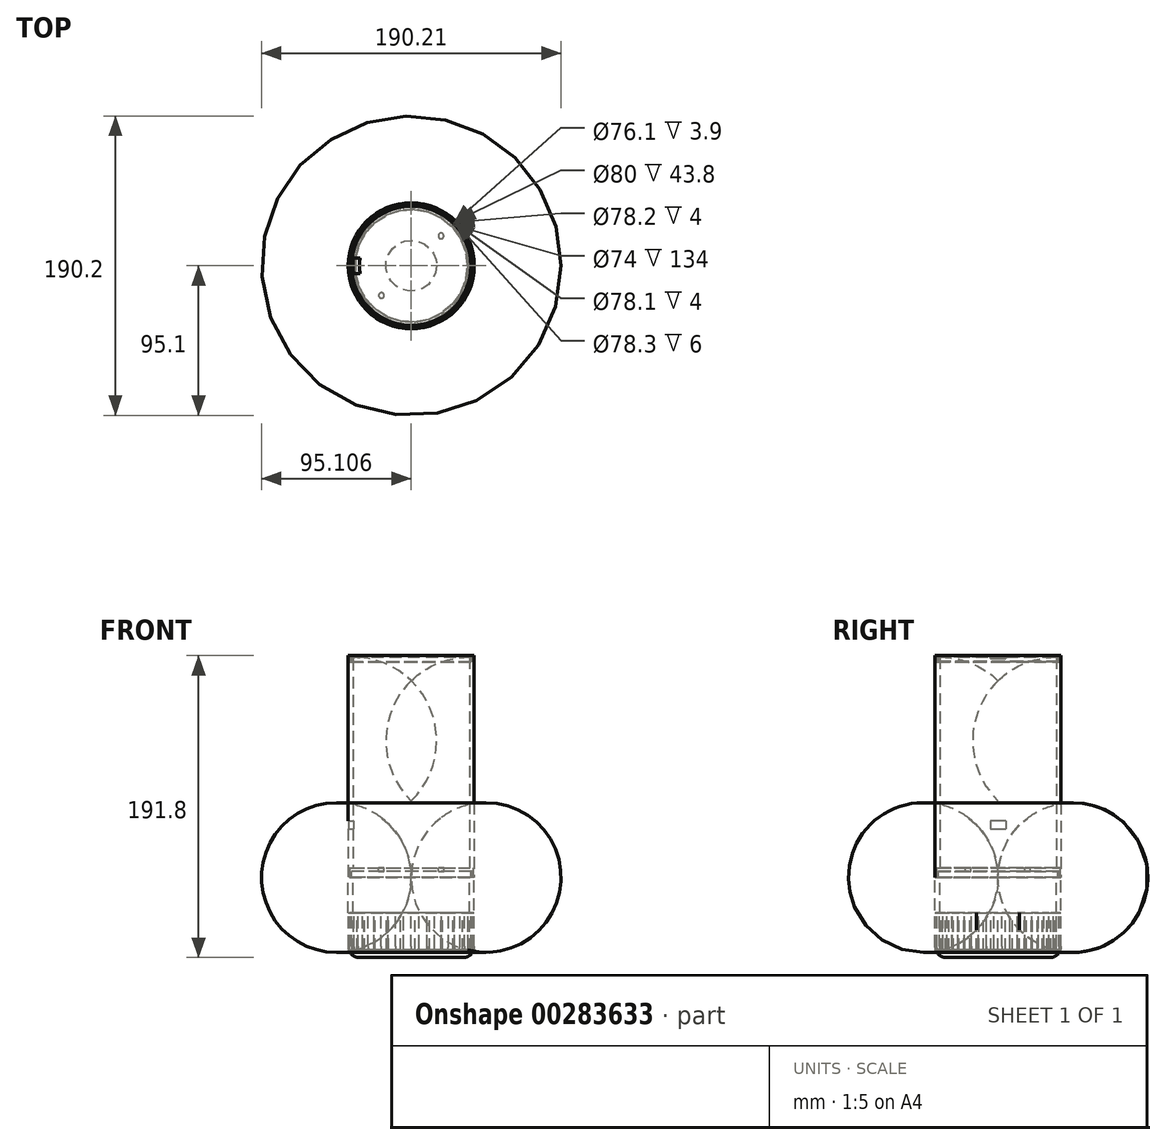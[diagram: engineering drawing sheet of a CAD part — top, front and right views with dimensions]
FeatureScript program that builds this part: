
annotation { "Feature Type Name" : "Feature", "Feature Type Description" : "" }
export const myFeature = defineFeature(function(context is Context, id is Id, definition is map)
    precondition{}
    {
        {
            var Q0;
            Q0=qCreatedBy(makeId("Front.planeOp"),FACE);
            var sketch = newSketch(context, id + "F0", { "sketchPlane" : qUnion([Q0])});
            skLineSegment(sketch, "E0", {"start": v(-47.53, -12.24) * mm, "end": v(-44.53, -12.24) * mm});
            skLineSegment(sketch, "E1", {"start": v(-44.53, -12.24) * mm, "end": v(-45.53, -12.24) * mm});
            skLineSegment(sketch, "E2", {"start": v(-44.53, -9) * mm, "end": v(-44.53, 127.76) * mm});
            skLineSegment(sketch, "E3", {"start": v(-47.53, 127.76) * mm, "end": v(-47.53, -10.24) * mm});
            skLineSegment(sketch, "E4", {"start": v(-47.53, -12.24) * mm, "end": v(-46.68, -12.24) * mm});
            skLineSegment(sketch, "E5", {"start": v(-7.53, -12.24) * mm, "end": v(-7.53, -63.04) * mm});
            skLineSegment(sketch, "E6", {"start": v(-44.53, -9) * mm, "end": v(-44.53, -12.24) * mm});
            skLineSegment(sketch, "E7", {"start": v(-46.68, -12.24) * mm, "end": v(-46.63, -12.24) * mm});
            skLineSegment(sketch, "E8", {"start": v(-46.63, -12.24) * mm, "end": v(-46.63, -8.24) * mm});
            skLineSegment(sketch, "E9", {"start": v(-45.38, -12.24) * mm, "end": v(-45.43, -12.24) * mm});
            skLineSegment(sketch, "E10", {"start": v(-45.43, -12.24) * mm, "end": v(-45.43, -8.24) * mm});
            skLineSegment(sketch, "E11", {"start": v(-45.43, -8.24) * mm, "end": v(-46.63, -8.24) * mm});
            skLineSegment(sketch, "E12", {"start": v(-47.53, -12.24) * mm, "end": v(-47.53, -56.04) * mm});
            skLineSegment(sketch, "E13", {"start": v(-7.53, -63.04) * mm, "end": v(-37.53, -63.04) * mm});
            skPoint(sketch, "E14.visualSharp", {"position": v(-47.53, -63.04) * mm});
            skArc(sketch, "E14.filletArc", {"start": v(-47.53, -56.04) * mm, "mid": v(-45.48, -61) * mm, "end": v(-40.53, -63.04) * mm});
            skLineSegment(sketch, "E15", {"start": v(-40.53, -63.04) * mm, "end": v(-37.53, -63.04) * mm});
            skLineSegment(sketch, "E16", {"start": v(-7.53, -63.04) * mm, "end": v(-7.53, -61.54) * mm});
            skLineSegment(sketch, "E17", {"start": v(-44.53, -12.24) * mm, "end": v(-44.53, -54.54) * mm});
            skLineSegment(sketch, "E18", {"start": v(-7.53, -61.54) * mm, "end": v(-37.53, -61.54) * mm});
            skArc(sketch, "E19.filletArc", {"start": v(-44.53, -54.54) * mm, "mid": v(-42.48, -59.5) * mm, "end": v(-37.53, -61.54) * mm});
            skLineSegment(sketch, "E20", {"start": v(-47.53, -10.24) * mm, "end": v(-47.53, -12.24) * mm});
            skPoint(sketch, "E21", {"position": v(-47.53, -34.14) * mm});
            skLineSegment(sketch, "E22", {"start": v(-47.53, -34.14) * mm, "end": v(-47.53, -46.54) * mm, "construction": true});
            skPoint(sketch, "E23", {"position": v(-47.53, -46.54) * mm});
            skLineSegment(sketch, "E24", {"start": v(-7.53, -63.04) * mm, "end": v(-7.53, 236.96) * mm, "construction": true});
            skLineSegment(sketch, "E25", {"start": v(-46.63, -8.24) * mm, "end": v(-46.63, -6.24) * mm});
            skLineSegment(sketch, "E26", {"start": v(-46.63, -6.24) * mm, "end": v(-7.53, -6.24) * mm});
            skLineSegment(sketch, "E27", {"start": v(-46.63, -8.24) * mm, "end": v(-45.38, -8.24) * mm});
            skPoint(sketch, "E27.endSnap0", {"position": v(-46.03, -8.24) * mm});
            skLineSegment(sketch, "E28", {"start": v(-45.38, -8.24) * mm, "end": v(-45.38, -12.24) * mm});
            skLineSegment(sketch, "E29", {"start": v(-45.38, -12.24) * mm, "end": v(-44.53, -12.24) * mm});
            skLineSegment(sketch, "E30", {"start": v(-44.53, -12.24) * mm, "end": v(-44.53, -8.24) * mm});
            skLineSegment(sketch, "E31", {"start": v(-44.53, -8.24) * mm, "end": v(-7.53, -8.24) * mm});
            skLineSegment(sketch, "E32", {"start": v(-7.53, -8.24) * mm, "end": v(-7.53, -6.24) * mm});
            skLineSegment(sketch, "E33", {"start": v(-46.68, -12.24) * mm, "end": v(-46.68, -6.24) * mm});
            skLineSegment(sketch, "E34", {"start": v(-46.68, -6.24) * mm, "end": v(-44.53, -6.24) * mm});
            skLineSegment(sketch, "E35", {"start": v(-47.53, 127.76) * mm, "end": v(-47.53, 128.76) * mm});
            skLineSegment(sketch, "E36", {"start": v(-47.53, 128.76) * mm, "end": v(-7.53, 128.76) * mm});
            skLineSegment(sketch, "E37", {"start": v(-7.53, 128.76) * mm, "end": v(-7.53, 127.76) * mm});
            skLineSegment(sketch, "E38", {"start": v(-7.53, 127.76) * mm, "end": v(-7.53, 112.76) * mm});
            skArc(sketch, "E39", {"start": v(-7.53, 112.76) * mm, "mid": v(-24.57, 123.86) * mm, "end": v(-44.53, 127.76) * mm});
            skLineSegment(sketch, "E40", {"start": v(-47.53, 128.76) * mm, "end": v(-46.58, 128.76) * mm});
            skLineSegment(sketch, "E41", {"start": v(-47.53, 128.76) * mm, "end": v(-46.68, 128.76) * mm});
            skLineSegment(sketch, "E42", {"start": v(-45.38, 127.76) * mm, "end": v(-44.53, 127.76) * mm});
            skLineSegment(sketch, "E43", {"start": v(-44.53, 127.76) * mm, "end": v(-44.53, 157.76) * mm});
            skLineSegment(sketch, "E44", {"start": v(-47.53, 128.76) * mm, "end": v(-47.53, 159.76) * mm});
            skLineSegment(sketch, "E45", {"start": v(-42.53, 164.76) * mm, "end": v(-7.53, 164.76) * mm});
            skLineSegment(sketch, "E46", {"start": v(-39.53, 162.76) * mm, "end": v(-7.53, 162.76) * mm});
            skLineSegment(sketch, "E47", {"start": v(-7.53, 162.76) * mm, "end": v(-7.53, 164.76) * mm});
            skPoint(sketch, "E48.visualSharp", {"position": v(-47.53, 164.76) * mm});
            skArc(sketch, "E48.filletArc", {"start": v(-42.53, 164.76) * mm, "mid": v(-46.07, 163.3) * mm, "end": v(-47.53, 159.76) * mm});
            skPoint(sketch, "E49.visualSharp", {"position": v(-44.53, 162.76) * mm});
            skArc(sketch, "E49.filletArc", {"start": v(-39.53, 162.76) * mm, "mid": v(-43.07, 161.3) * mm, "end": v(-44.53, 157.76) * mm});
            skLineSegment(sketch, "E50", {"start": v(-44.53, 157.76) * mm, "end": v(-44.53, 144.76) * mm});
            skPoint(sketch, "E51", {"position": v(-44.53, 144.76) * mm});
            skLineSegment(sketch, "E52.MirrorCS", {"start": v(-46.58, 128.76) * mm, "end": v(-46.58, 124.76) * mm});
            skLineSegment(sketch, "E53.MirrorCS", {"start": v(-46.58, 124.76) * mm, "end": v(-45.48, 124.76) * mm});
            skLineSegment(sketch, "E54.MirrorCS", {"start": v(-45.48, 124.76) * mm, "end": v(-45.48, 128.76) * mm});
            skLineSegment(sketch, "E55.MirrorCS", {"start": v(-46.68, 124.66) * mm, "end": v(-45.38, 124.66) * mm});
            skLineSegment(sketch, "E56", {"start": v(-44.53, 127.76) * mm, "end": v(-44.53, 132.76) * mm});
            skPoint(sketch, "E57", {"position": v(-44.53, 132.76) * mm});
            skLineSegment(sketch, "E58", {"start": v(-44.53, -6.24) * mm, "end": v(-44.53, 23.76) * mm});
            skPoint(sketch, "E59", {"position": v(-44.53, 23.76) * mm});
            skLineSegment(sketch, "E60", {"start": v(-46.58, 128.76) * mm, "end": v(-46.48, 128.76) * mm});
            skLineSegment(sketch, "E61", {"start": v(-46.48, 128.76) * mm, "end": v(-46.48, 124.86) * mm});
            skLineSegment(sketch, "E62", {"start": v(-46.48, 124.86) * mm, "end": v(-45.58, 124.86) * mm});
            skLineSegment(sketch, "E63", {"start": v(-45.58, 124.86) * mm, "end": v(-45.58, 128.76) * mm});
            skLineSegment(sketch, "E64", {"start": v(-7.53, -59.5) * mm, "end": v(-7.53, -52.5) * mm});
            skLineSegment(sketch, "E65", {"start": v(-42.48, -59.5) * mm, "end": v(-39.8, -59.5) * mm});
            skLineSegment(sketch, "E66", {"start": v(-7.53, -59.5) * mm, "end": v(-69.7, -59.5) * mm, "construction": true});
            skPoint(sketch, "E66.endSnap0", {"position": v(-41.15, -59.5) * mm});
            skLineSegment(sketch, "E67", {"start": v(-42.48, -59.5) * mm, "end": v(-49.48, -59.5) * mm, "construction": true});
            skLineSegment(sketch, "E68", {"start": v(-49.48, -59.5) * mm, "end": v(-42.58, -58.34) * mm, "construction": true});
            skLineSegment(sketch, "E69", {"start": v(-49.48, -59.5) * mm, "end": v(-44.48, -59.5) * mm, "construction": true});
            skLineSegment(sketch, "E70", {"start": v(-44.48, -59.5) * mm, "end": v(-39.48, -59.5) * mm, "construction": true});
            skLineSegment(sketch, "E71", {"start": v(-39.48, -59.5) * mm, "end": v(-34.48, -59.5) * mm, "construction": true});
            skLineSegment(sketch, "E72", {"start": v(-34.48, -59.5) * mm, "end": v(-29.48, -59.5) * mm, "construction": true});
            skLineSegment(sketch, "E73", {"start": v(-29.48, -59.5) * mm, "end": v(-24.48, -59.5) * mm, "construction": true});
            skLineSegment(sketch, "E74", {"start": v(-24.48, -59.5) * mm, "end": v(-19.48, -59.5) * mm, "construction": true});
            skLineSegment(sketch, "E75", {"start": v(-19.48, -59.5) * mm, "end": v(-14.48, -59.5) * mm, "construction": true});
            skLineSegment(sketch, "E76", {"start": v(-14.48, -59.5) * mm, "end": v(-9.48, -59.5) * mm, "construction": true});
            skLineSegment(sketch, "E77", {"start": v(-44.48, -59.5) * mm, "end": v(-37.6, -58.2) * mm, "construction": true});
            skLineSegment(sketch, "E78", {"start": v(-39.48, -59.5) * mm, "end": v(-32.65, -58) * mm, "construction": true});
            skLineSegment(sketch, "E79", {"start": v(-34.48, -59.5) * mm, "end": v(-27.7, -57.73) * mm, "construction": true});
            skLineSegment(sketch, "E80", {"start": v(-29.48, -59.5) * mm, "end": v(-22.81, -57.37) * mm, "construction": true});
            skLineSegment(sketch, "E81", {"start": v(-24.48, -59.5) * mm, "end": v(-18.01, -56.82) * mm, "construction": true});
            skLineSegment(sketch, "E82", {"start": v(-19.48, -59.5) * mm, "end": v(-13.44, -55.96) * mm, "construction": true});
            skLineSegment(sketch, "E83", {"start": v(-14.48, -59.5) * mm, "end": v(-9.55, -54.53) * mm, "construction": true});
            skLineSegment(sketch, "E84", {"start": v(-9.48, -59.5) * mm, "end": v(-7.6, -52.75) * mm, "construction": true});
            skLineSegment(sketch, "E85", {"start": v(-9.48, -59.5) * mm, "end": v(-11.48, -59.5) * mm, "construction": true});
            skLineSegment(sketch, "E86", {"start": v(-11.48, -59.5) * mm, "end": v(-13.48, -59.5) * mm, "construction": true});
            skLineSegment(sketch, "E87", {"start": v(-13.48, -59.5) * mm, "end": v(-15.48, -59.5) * mm, "construction": true});
            skLineSegment(sketch, "E88", {"start": v(-15.48, -59.5) * mm, "end": v(-17.48, -59.5) * mm, "construction": true});
            skLineSegment(sketch, "E89", {"start": v(-17.48, -59.5) * mm, "end": v(-19.48, -59.5) * mm, "construction": true});
            skLineSegment(sketch, "E90", {"start": v(-19.48, -59.5) * mm, "end": v(-21.48, -59.5) * mm, "construction": true});
            skLineSegment(sketch, "E91", {"start": v(-21.48, -59.5) * mm, "end": v(-23.48, -59.5) * mm, "construction": true});
            skLineSegment(sketch, "E92", {"start": v(-23.48, -59.5) * mm, "end": v(-17.07, -56.68) * mm, "construction": true});
            skLineSegment(sketch, "E93", {"start": v(-21.48, -59.5) * mm, "end": v(-15.23, -56.35) * mm, "construction": true});
            skLineSegment(sketch, "E94", {"start": v(-17.48, -59.5) * mm, "end": v(-11.76, -55.47) * mm, "construction": true});
            skLineSegment(sketch, "E95", {"start": v(-15.48, -59.5) * mm, "end": v(-10.23, -54.87) * mm, "construction": true});
            skLineSegment(sketch, "E96", {"start": v(-13.48, -59.5) * mm, "end": v(-8.95, -54.16) * mm, "construction": true});
            skLineSegment(sketch, "E97", {"start": v(-11.48, -59.5) * mm, "end": v(-8.04, -53.4) * mm, "construction": true});
            skPoint(sketch, "E98", {"position": v(-43.41, -58.34) * mm});
            skArc(sketch, "E99", {"start": v(-43.41, -58.34) * mm, "mid": v(-17.56, -41.45) * mm, "end": v(-7.53, -12.24) * mm});
            skSolve(sketch);
        }
        {
            var Q0;
            {var subQ1=sQuery(id+"F0.wireOp",EDGE,"E0");Q0=makeQuery(id+"F0.imprint","IMPRINT",FACE,{"disambiguationData":[TD([[makeQuery(id+"F0.imprint","IMPRINT",EDGE,{"derivedFrom":subQ1}),1.0]])]});}
            var Q1;
            {var subQ1=sQuery(id+"F0.wireOp",EDGE,"E0");Q1=makeQuery(id+"F0.imprint","IMPRINT",FACE,{"disambiguationData":[TD([[makeQuery(id+"F0.imprint","IMPRINT",EDGE,{"derivedFrom":subQ1}),-1.0]])]});}
            var Q2;
            Q2=makeQuery(id+"F0.imprint","IMPRINT",FACE,{"disambiguationData":[TD([[makeQuery(id+"F0.imprint","IMPRINT",EDGE,{"derivedFrom":sQuery(id+"F0.wireOp",EDGE,"E5")}),-1.0]])]});
            var Q3;
            Q3=sQuery(id+"F0.wireOp",EDGE,"E5");
            revolve(context, id + "F1", {"entities" : qUnion([Q0, Q1, Q2]), "axis" : qUnion([Q3]), "revolveType" : RevolveType.FULL});
        }
        {
            var Q0;
            Q0=sQuery(id+"F0.wireOp",EDGE,"E12");
            var Q1;
            Q1=sQuery(id+"F0.wireOp",VERTEX,"E23");
            cPlane(context, id + "F2", {"entities" : qUnion([Q0, Q1]), "cplaneType" : CPlaneType.LINE_POINT, "offset" : 0 * mm, "width" : 150 * mm, "height" : 150 * mm});
        }
        {
            var Q0;
            Q0=qCreatedBy(id+"F2.planeOp",FACE);
            var sketch = newSketch(context, id + "F3", { "sketchPlane" : qUnion([Q0])});
            skLineSegment(sketch, "E100", {"start": v(-47.53, 0) * mm, "end": v(-43.03, 0) * mm, "construction": true});
            skLineSegment(sketch, "E101", {"start": v(-43.03, 0) * mm, "end": v(-43.03, 2.5) * mm, "construction": true});
            skLineSegment(sketch, "E102", {"start": v(-43.03, 2.5) * mm, "end": v(-47.53, 2.5) * mm});
            skLineSegment(sketch, "E103", {"start": v(-47.53, 2.5) * mm, "end": v(-47.53, -2.5) * mm});
            skLineSegment(sketch, "E104", {"start": v(-47.53, -2.5) * mm, "end": v(-43.03, -2.5) * mm});
            skLineSegment(sketch, "E105", {"start": v(-43.03, -2.5) * mm, "end": v(-43.03, 2.5) * mm});
            skLineSegment(sketch, "E106", {"start": v(-43.03, -6.5) * mm, "end": v(-43.03, -2.5) * mm});
            skLineSegment(sketch, "E107.MirrorCS", {"start": v(-43.03, 6.5) * mm, "end": v(-43.03, 2.5) * mm});
            skLineSegment(sketch, "E108", {"start": v(-43.03, -2.5) * mm, "end": v(-44.13, -2.5) * mm, "construction": true});
            skLineSegment(sketch, "E109", {"start": v(-44.13, -2.5) * mm, "end": v(-44.13, -5.3) * mm, "construction": true});
            skArc(sketch, "E110", {"start": v(-44.13, -5.3) * mm, "mid": v(-45.33, -3.3) * mm, "end": v(-47.53, -2.5) * mm});
            skArc(sketch, "E111", {"start": v(-44.13, -5.3) * mm, "mid": v(-43.82, -6.11) * mm, "end": v(-43.03, -6.5) * mm});
            skArc(sketch, "E112.MirrorCS", {"start": v(-44.13, 5.3) * mm, "mid": v(-45.33, 3.3) * mm, "end": v(-47.53, 2.5) * mm});
            skArc(sketch, "E113.MirrorCS", {"start": v(-44.13, 5.3) * mm, "mid": v(-43.82, 6.11) * mm, "end": v(-43.03, 6.5) * mm});
            skSolve(sketch);
        }
        {
            var Q0;
            Q0 = qSketchRegion(id + "F3", true);
            extrude(context, id + "F4", {"entities" : qUnion([Q0]), "endBound" : BoundingType.SYMMETRIC, "depth" : 23.6 * mm});
        }
        {
            var Q0;
            Q0=makeQuery(id+"F4.opExtrude","SWEPT_BODY",BODY,{"disambiguationData":[OSD([sQuery(id+"F3.wireOp",EDGE,"E102"),sQuery(id+"F3.wireOp",EDGE,"E103"),sQuery(id+"F3.wireOp",EDGE,"E104"),sQuery(id+"F3.wireOp",EDGE,"E105")])]});
            var Q1;
            Q1=sQuery(id+"F0.wireOp",EDGE,"E5");
            circularPattern(context, id + "F5", {"operationType" : NewBodyOperationType.REMOVE, "entities" : qUnion([Q0]), "axis" : qUnion([Q1]), "angle" : 360 * degree, "instanceCount" : 25, "equalSpace" : true});
        }
        {
            var Q0;
            Q0=makeQuery(id+"F0.imprint","IMPRINT",FACE,{"disambiguationData":[TD([[makeQuery(id+"F0.imprint","IMPRINT",EDGE,{"derivedFrom":sQuery(id+"F0.wireOp",EDGE,"E2")}),1.0]])]});
            var Q1;
            {var subQ2=sQuery(id+"F0.wireOp",EDGE,"E26");Q1=makeQuery(id+"F0.imprint","IMPRINT",FACE,{"disambiguationData":[TD([[makeQuery(id+"F0.imprint","IMPRINT",EDGE,{"derivedFrom":subQ2}),-1.0]])]});}
            var Q2;
            Q2=sQuery(id+"F0.wireOp",EDGE,"E5");
            revolve(context, id + "F6", {"entities" : qUnion([Q0, Q1]), "axis" : qUnion([Q2]), "revolveType" : RevolveType.FULL});
        }
        {
            var Q0;
            Q0=makeQuery(id+"F0.imprint","IMPRINT",FACE,{"disambiguationData":[TD([[makeQuery(id+"F0.imprint","IMPRINT",EDGE,{"derivedFrom":sQuery(id+"F0.wireOp",EDGE,"E3")}),1.0]])]});
            var Q1;
            {var subQ1=sQuery(id+"F0.wireOp",EDGE,"E37");Q1=makeQuery(id+"F0.imprint","IMPRINT",FACE,{"disambiguationData":[TD([[makeQuery(id+"F0.imprint","IMPRINT",EDGE,{"derivedFrom":subQ1}),-1.0]])]});}
            var Q2;
            Q2=sQuery(id+"F0.wireOp",EDGE,"E24");
            revolve(context, id + "F7", {"entities" : qUnion([Q0, Q1]), "axis" : qUnion([Q2]), "revolveType" : RevolveType.FULL});
        }
        {
            var Q0;
            Q0=makeQuery(id+"F0.imprint","IMPRINT",FACE,{"disambiguationData":[TD([[makeQuery(id+"F0.imprint","IMPRINT",EDGE,{"derivedFrom":sQuery(id+"F0.wireOp",EDGE,"E41")}),1.0]])]});
            var Q1;
            {var subQ0=sQuery(id+"F0.wireOp",EDGE,"E61");Q1=makeQuery(id+"F0.imprint","IMPRINT",FACE,{"disambiguationData":[TD([[makeQuery(id+"F0.imprint","IMPRINT",EDGE,{"derivedFrom":subQ0}),1.0]])]});}
            var Q2;
            Q2=sQuery(id+"F0.wireOp",EDGE,"E24");
            revolve(context, id + "F8", {"entities" : qUnion([Q0, Q1]), "axis" : qUnion([Q2]), "revolveType" : RevolveType.FULL});
        }
        {
            var Q0;
            Q0=sQuery(id+"F0.wireOp",EDGE,"E43");
            cPlane(context, id + "F9", {"entities" : qUnion([Q0]), "cplaneType" : CPlaneType.LINE_ANGLE, "offset" : 25 * mm, "angle" : 0 * degree, "width" : 150 * mm, "height" : 150 * mm});
        }
        {
            var Q0;
            Q0=qCreatedBy(id+"F9.planeOp",FACE);
            var sketch = newSketch(context, id + "F10", { "sketchPlane" : qUnion([Q0])});
            skLineSegment(sketch, "E114", {"start": v(0, 144.76) * mm, "end": v(2, 144.76) * mm});
            skLineSegment(sketch, "E115.bottom", {"start": v(2, 144.76) * mm, "end": v(0, 144.76) * mm});
            skLineSegment(sketch, "E116", {"start": v(0, 23.76) * mm, "end": v(-5, 23.76) * mm});
            skLineSegment(sketch, "E117.bottom", {"start": v(-5, 23.76) * mm, "end": v(5, 23.76) * mm});
            skLineSegment(sketch, "E117.top", {"start": v(-5, 18.76) * mm, "end": v(5, 18.76) * mm});
            skLineSegment(sketch, "E117.left", {"start": v(-5, 23.76) * mm, "end": v(-5, 18.76) * mm});
            skLineSegment(sketch, "E117.right", {"start": v(5, 23.76) * mm, "end": v(5, 18.76) * mm});
            skLineSegment(sketch, "E118", {"start": v(0, 144.76) * mm, "end": v(-2, 144.76) * mm});
            skLineSegment(sketch, "E119.bottom", {"start": v(-2, 144.76) * mm, "end": v(2, 144.76) * mm});
            skLineSegment(sketch, "E119.top", {"start": v(-2, 162.66) * mm, "end": v(2, 162.66) * mm});
            skLineSegment(sketch, "E119.left", {"start": v(-2, 144.76) * mm, "end": v(-2, 162.66) * mm});
            skLineSegment(sketch, "E119.right", {"start": v(2, 144.76) * mm, "end": v(2, 162.66) * mm});
            skSolve(sketch);
        }
        {
            var Q0;
            Q0=qSketchRegion(id+"F10",true);
            extrude(context, id + "F11", {"entities" : qUnion([Q0]), "endBound" : BoundingType.SYMMETRIC, "oppositeDirection" : true, "depth" : 8 * mm});
        }
        {
            var Q0;
            Q0=makeQuery(id+"F11.opExtrude","SWEPT_BODY",BODY,{"disambiguationData":[OSD([sQuery(id+"F10.wireOp",EDGE,"E119.bottom"),sQuery(id+"F10.wireOp",EDGE,"E119.top"),sQuery(id+"F10.wireOp",EDGE,"E119.left"),sQuery(id+"F10.wireOp",EDGE,"E119.right")])]});
            var Q1;
            Q1=sQuery(id+"F0.wireOp",EDGE,"E24");
            circularPattern(context, id + "F12", {"operationType" : NewBodyOperationType.REMOVE, "entities" : qUnion([Q0]), "axis" : qUnion([Q1]), "angle" : 360 * degree, "instanceCount" : 25, "equalSpace" : true});
        }
        {
            var Q0;
            Q0=makeQuery(id+"F6.opRevolve","SWEPT_FACE",FACE,{"disambiguationData":[OSD([sQuery(id+"F0.wireOp",EDGE,"E26"),sQuery(id+"F0.wireOp",EDGE,"E34")])]});
            var sketch = newSketch(context, id + "F13", { "sketchPlane" : qUnion([Q0])});
            skPoint(sketch, "E120", {"position": v(-7.53, 0) * mm});
            skCircle(sketch, "E121", {"center": v(-7.53, 0) * mm, "radius": 25 * mm});
            skLineSegment(sketch, "E122", {"start": v(-7.53, 0) * mm, "end": v(-46.63, 0) * mm, "construction": true});
            skLineSegment(sketch, "E123", {"start": v(-46.63, 0) * mm, "end": v(-7.53, 0) * mm, "construction": true});
            skLineSegment(sketch, "E124", {"start": v(-7.53, 0) * mm, "end": v(31.57, 0) * mm, "construction": true});
            skLineSegment(sketch, "E125", {"start": v(-7.53, 0) * mm, "end": v(-7.53, 39.1) * mm, "construction": true});
            skLineSegment(sketch, "E126", {"start": v(-7.53, 0) * mm, "end": v(-7.53, -39.1) * mm, "construction": true});
            skLineSegment(sketch, "E127", {"start": v(-7.53, 39.1) * mm, "end": v(31.57, 0) * mm, "construction": true});
            skLineSegment(sketch, "E128", {"start": v(31.57, 0) * mm, "end": v(-7.53, -39.1) * mm, "construction": true});
            skLineSegment(sketch, "E129", {"start": v(-7.53, -39.1) * mm, "end": v(-46.63, 0) * mm, "construction": true});
            skLineSegment(sketch, "E130", {"start": v(-46.63, 0) * mm, "end": v(-7.53, 39.1) * mm, "construction": true});
            skLineSegment(sketch, "E131", {"start": v(-7.53, 0) * mm, "end": v(20.11, 27.65) * mm, "construction": true});
            skLineSegment(sketch, "E132", {"start": v(-7.53, 0) * mm, "end": v(-35.18, -27.65) * mm, "construction": true});
            skLineSegment(sketch, "E133", {"start": v(-7.53, 0) * mm, "end": v(-35.18, 27.65) * mm, "construction": true});
            skLineSegment(sketch, "E134", {"start": v(-7.53, 0) * mm, "end": v(20.11, -27.65) * mm, "construction": true});
            skLineSegment(sketch, "E135", {"start": v(-25.21, 17.68) * mm, "end": v(-26.46, 18.92) * mm, "construction": true});
            skCircle(sketch, "E136", {"center": v(-26.46, 18.92) * mm, "radius": 1.75 * mm});
            skCircle(sketch, "E137.MirrorC", {"center": v(11.39, 18.92) * mm, "radius": 1.75 * mm});
            skCircle(sketch, "E138.MirrorC", {"center": v(-26.46, -18.92) * mm, "radius": 1.75 * mm});
            skCircle(sketch, "E139.MirrorC", {"center": v(11.39, -18.92) * mm, "radius": 1.75 * mm});
            skSolve(sketch);
        }
        {
            var Q0;
            Q0=makeQuery(id+"F13.imprint","IMPRINT",FACE,{"disambiguationData":[TD([[makeQuery(id+"F13.imprint","IMPRINT",EDGE,{"derivedFrom":sQuery(id+"F13.wireOp",EDGE,"E136")}),1.0]])]});
            var Q1;
            {var subQ0=sQuery(id+"F13.wireOp",EDGE,"E121");var subQ1=makeQuery(id+"F13.imprint","INTERSECT",VERTEX,{"derivedFrom":[subQ0,sQuery(id+"F13.wireOp",EDGE,"E136")]});Q1=makeQuery(id+"F13.imprint","IMPRINT",FACE,{"disambiguationData":[TD([[makeQuery(id+"F13.imprint","IMPRINT",EDGE,{"disambiguationData":[TD([[subQ1,1.0]])],"derivedFrom":subQ0}),1.0]])]});}
            var Q2;
            Q2=makeQuery(id+"F13.imprint","IMPRINT",FACE,{"disambiguationData":[TD([[makeQuery(id+"F13.imprint","IMPRINT",EDGE,{"derivedFrom":sQuery(id+"F13.wireOp",EDGE,"E137.MirrorC")}),-1.0]])]});
            var Q3;
            Q3=makeQuery(id+"F13.imprint","IMPRINT",FACE,{"disambiguationData":[TD([[makeQuery(id+"F13.imprint","IMPRINT",EDGE,{"derivedFrom":sQuery(id+"F13.wireOp",EDGE,"E139.MirrorC")}),1.0]])]});
            var Q4;
            Q4=makeQuery(id+"F13.imprint","IMPRINT",FACE,{"disambiguationData":[TD([[makeQuery(id+"F13.imprint","IMPRINT",EDGE,{"derivedFrom":sQuery(id+"F13.wireOp",EDGE,"E138.MirrorC")}),-1.0]])]});
            var Q5;
            Q5=makeQuery(id+"F13.imprint","IMPRINT",FACE,{"disambiguationData":[TD([[makeQuery(id+"F13.imprint","IMPRINT",EDGE,{"derivedFrom":sQuery(id+"F13.wireOp",EDGE,"E121")}),1.0]])]});
            extrude(context, id + "F14", {"entities" : qUnion([Q0, Q1, Q2, Q3, Q4, Q5]), "operationType" : NewBodyOperationType.REMOVE, "endBound" : BoundingType.UP_TO_NEXT, "oppositeDirection" : true, "depth" : 25 * mm});
        }
        {
            var Q0;
            Q0=makeQuery(id+"F10.imprint","IMPRINT",FACE,{"disambiguationData":[TD([[makeQuery(id+"F10.imprint","IMPRINT",EDGE,{"derivedFrom":sQuery(id+"F10.wireOp",EDGE,"E117.top")}),1.0]])]});
            var Q1;
            Q1=makeQuery(id+"F10.imprint","IMPRINT",FACE,{"disambiguationData":[TD([[makeQuery(id+"F10.imprint","IMPRINT",EDGE,{"derivedFrom":sQuery(id+"F10.wireOp",EDGE,"J7AmGKRm-i65D-M9V7-LQzS-6A68N8WfuHxk.top")}),1.0]])]});
            extrude(context, id + "F15", {"entities" : qUnion([Q0, Q1]), "operationType" : NewBodyOperationType.REMOVE, "endBound" : BoundingType.SYMMETRIC, "oppositeDirection" : true, "depth" : 8 * mm});
        }
        {
            var Q0;
            Q0=makeQuery(id+"F7.opRevolve","SWEPT_FACE",FACE,{"disambiguationData":[OSD([sQuery(id+"F0.wireOp",EDGE,"E36"),sQuery(id+"F0.wireOp",EDGE,"E42")])]});
            var sketch = newSketch(context, id + "F16", { "sketchPlane" : qUnion([Q0])});
            skLineSegment(sketch, "E140", {"start": v(-45.48, 0) * mm, "end": v(-42.48, 0) * mm});
            skLineSegment(sketch, "E141", {"start": v(-45.48, 0) * mm, "end": v(-7.53, 0) * mm, "construction": true});
            skCircle(sketch, "E142", {"center": v(-7.53, 0) * mm, "radius": 32.85 * mm});
            skLineSegment(sketch, "E143", {"start": v(-40, 5) * mm, "end": v(-45.15, 5) * mm});
            skLineSegment(sketch, "E144", {"start": v(-40, -5) * mm, "end": v(-45.15, -5) * mm});
            skSolve(sketch);
        }
        {
            var Q0;
            {var subQ2=sQuery(id+"F16.wireOp",EDGE,"E143");Q0=makeQuery(id+"F16.imprint","IMPRINT",FACE,{"disambiguationData":[TD([[makeQuery(id+"F16.imprint","IMPRINT",EDGE,{"derivedFrom":subQ2}),1.0]])]});}
            extrude(context, id + "F17", {"entities" : qUnion([Q0]), "operationType" : NewBodyOperationType.REMOVE, "oppositeDirection" : true, "depth" : 2 * mm});
        }
    });
